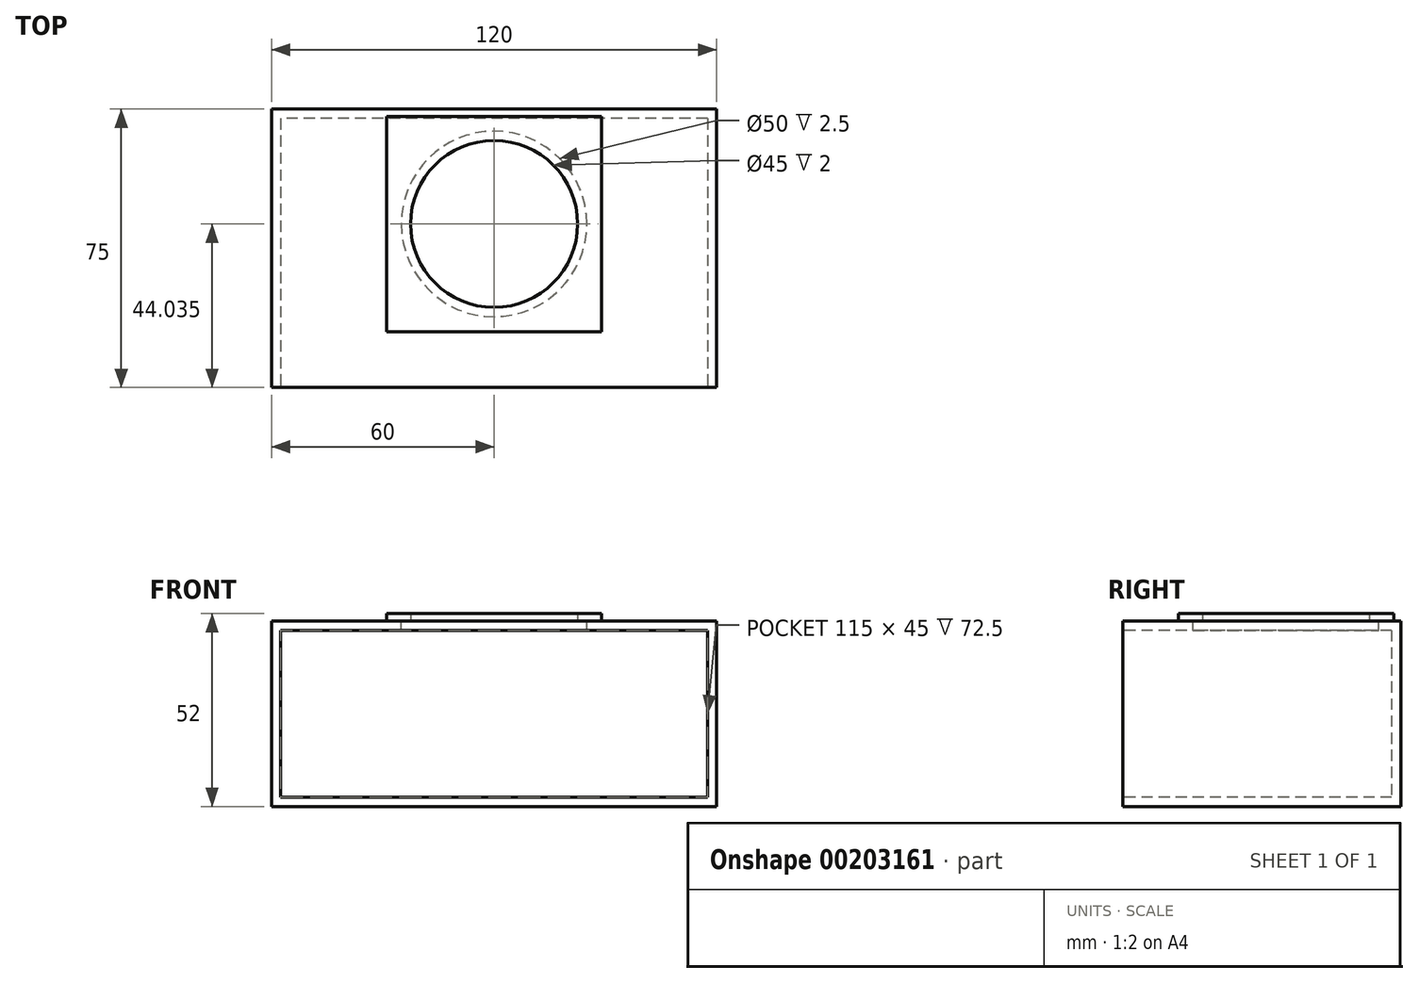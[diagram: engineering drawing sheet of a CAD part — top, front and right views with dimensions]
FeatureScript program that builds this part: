
annotation { "Feature Type Name" : "Feature", "Feature Type Description" : "" }
export const myFeature = defineFeature(function(context is Context, id is Id, definition is map)
    precondition{}
    {
        {
            var Q0;
            Q0=qCreatedBy(makeId("Front.planeOp"),FACE);
            var sketch = newSketch(context, id + "F0", { "sketchPlane" : qUnion([Q0])});
            skLineSegment(sketch, "E0.bottom", {"start": v(60, 25) * mm, "end": v(-60, 25) * mm});
            skLineSegment(sketch, "E0.top", {"start": v(60, -25) * mm, "end": v(-60, -25) * mm});
            skLineSegment(sketch, "E0.left", {"start": v(60, 25) * mm, "end": v(60, -25) * mm});
            skLineSegment(sketch, "E0.right", {"start": v(-60, 25) * mm, "end": v(-60, -25) * mm});
            skPoint(sketch, "E0.middle", {"position": v(0, 0) * mm});
            skSolve(sketch);
        }
        {
            var Q0;
            Q0 = qSketchRegion(id + "F0", true);
            extrude(context, id + "F1", {"entities" : qUnion([Q0]), "oppositeDirection" : true, "depth" : 75 * mm});
        }
        {
            var Q0;
            Q0=makeQuery(id+"F1.opExtrude","CAP_FACE",FACE,{"disambiguationData":[OSD([sQuery(id+"F0.wireOp",EDGE,"E0.bottom"),sQuery(id+"F0.wireOp",EDGE,"E0.top"),sQuery(id+"F0.wireOp",EDGE,"E0.left"),sQuery(id+"F0.wireOp",EDGE,"E0.right")])],"isStart":true});
            shell(context, id + "F2", {"entities" : qUnion([Q0]), "thickness" : 2.5 * mm});
        }
        {
            var Q0;
            Q0=makeQuery(id+"F1.opExtrude","SWEPT_FACE",FACE,{"disambiguationData":[OSD([sQuery(id+"F0.wireOp",EDGE,"E0.bottom")])]});
            var sketch = newSketch(context, id + "F3", { "sketchPlane" : qUnion([Q0])});
            skLineSegment(sketch, "E1.bottom", {"start": v(25, 69.04) * mm, "end": v(-25, 69.04) * mm, "construction": true});
            skLineSegment(sketch, "E1.top", {"start": v(25, 19.04) * mm, "end": v(-25, 19.04) * mm, "construction": true});
            skLineSegment(sketch, "E1.left", {"start": v(25, 69.04) * mm, "end": v(25, 19.04) * mm, "construction": true});
            skLineSegment(sketch, "E1.right", {"start": v(-25, 69.04) * mm, "end": v(-25, 19.04) * mm, "construction": true});
            skPoint(sketch, "E1.middle", {"position": v(0, 44.04) * mm});
            skCircle(sketch, "E2", {"center": v(0, 44.04) * mm, "radius": 25 * mm});
            skPoint(sketch, "E3", {"position": v(-25, 69.04) * mm});
            skPoint(sketch, "E4", {"position": v(25, 69.04) * mm});
            skPoint(sketch, "E5", {"position": v(25, 19.04) * mm});
            skPoint(sketch, "E6", {"position": v(-25, 19.04) * mm});
            skSolve(sketch);
        }
        {
            var Q0;
            Q0 = qSketchRegion(id + "F3", true);
            extrude(context, id + "F4", {"entities" : qUnion([Q0]), "operationType" : NewBodyOperationType.REMOVE, "endBound" : BoundingType.UP_TO_NEXT, "oppositeDirection" : true, "depth" : 25 * mm});
        }
        {
            var Q0;
            Q0=makeQuery(id+"F1.opExtrude","SWEPT_FACE",FACE,{"disambiguationData":[OSD([sQuery(id+"F0.wireOp",EDGE,"E0.bottom")])]});
            var sketch = newSketch(context, id + "F5", { "sketchPlane" : qUnion([Q0])});
            skLineSegment(sketch, "E7.bottom", {"start": v(-25, 69.04) * mm, "end": v(25, 69.04) * mm, "construction": true});
            skLineSegment(sketch, "E7.top", {"start": v(-25, 19.04) * mm, "end": v(25, 19.04) * mm, "construction": true});
            skLineSegment(sketch, "E7.left", {"start": v(-25, 69.04) * mm, "end": v(-25, 19.04) * mm, "construction": true});
            skLineSegment(sketch, "E7.right", {"start": v(25, 69.04) * mm, "end": v(25, 19.04) * mm, "construction": true});
            skCircle(sketch, "E8", {"center": v(0, 44.04) * mm, "radius": 22.5 * mm});
            skLineSegment(sketch, "E9.0", {"start": v(-29, 73.04) * mm, "end": v(29, 73.04) * mm});
            skLineSegment(sketch, "E9.1", {"start": v(-29, 73.04) * mm, "end": v(-29, 15.04) * mm});
            skLineSegment(sketch, "E9.2", {"start": v(-29, 15.04) * mm, "end": v(29, 15.04) * mm});
            skLineSegment(sketch, "E9.3", {"start": v(29, 73.04) * mm, "end": v(29, 15.04) * mm});
            skSolve(sketch);
        }
        {
            var Q0;
            Q0 = qSketchRegion(id + "F5", true);
            extrude(context, id + "F6", {"entities" : qUnion([Q0]), "operationType" : NewBodyOperationType.ADD, "depth" : 2 * mm});
        }
    });
